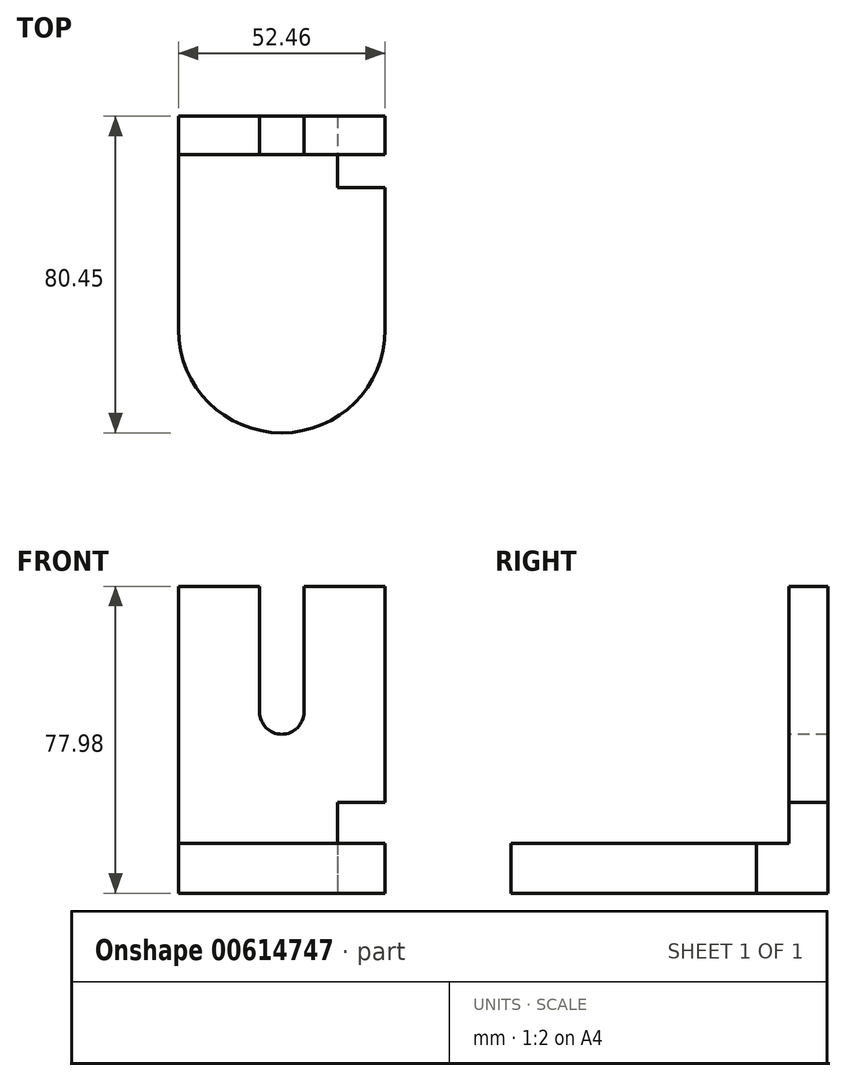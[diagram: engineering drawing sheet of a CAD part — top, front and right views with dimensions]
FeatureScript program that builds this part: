
annotation { "Feature Type Name" : "Feature", "Feature Type Description" : "" }
export const myFeature = defineFeature(function(context is Context, id is Id, definition is map)
    precondition{}
    {
        {
            var Q0;
            Q0=qCreatedBy(makeId("Top.planeOp"),FACE);
            var sketch = newSketch(context, id + "F0", { "sketchPlane" : qUnion([Q0])});
            skLineSegment(sketch, "E0.bottom", {"start": v(26.23, -27.11) * mm, "end": v(-26.23, -27.11) * mm});
            skLineSegment(sketch, "E0.top", {"start": v(26.23, 27.11) * mm, "end": v(-26.23, 27.11) * mm});
            skLineSegment(sketch, "E0.left", {"start": v(26.23, -27.11) * mm, "end": v(26.23, 27.11) * mm});
            skLineSegment(sketch, "E0.right", {"start": v(-26.23, -27.11) * mm, "end": v(-26.23, 27.11) * mm});
            skPoint(sketch, "E0.middle", {"position": v(0, 0) * mm});
            skArc(sketch, "E1", {"start": v(-26.23, -27.11) * mm, "mid": v(0, -53.34) * mm, "end": v(26.23, -27.11) * mm});
            skSolve(sketch);
        }
        {
            var Q0;
            Q0=makeQuery(id+"F0.imprint","IMPRINT",FACE,{"disambiguationData":[TD([[makeQuery(id+"F0.imprint","IMPRINT",EDGE,{"derivedFrom":sQuery(id+"F0.wireOp",EDGE,"E0.bottom")}),-1.0]])]});
            var sketch = newSketch(context, id + "F1", { "sketchPlane" : qUnion([Q0])});
            skSolve(sketch);
        }
        {
            var Q0;
            Q0 = qSketchRegion(id + "F1", true);
            var Q1;
            Q1=makeQuery(id+"F0.imprint","IMPRINT",FACE,{"disambiguationData":[TD([[makeQuery(id+"F0.imprint","IMPRINT",EDGE,{"derivedFrom":sQuery(id+"F0.wireOp",EDGE,"E0.bottom")}),1.0]])]});
            var Q2;
            Q2=makeQuery(id+"F0.imprint","IMPRINT",FACE,{"disambiguationData":[TD([[makeQuery(id+"F0.imprint","IMPRINT",EDGE,{"derivedFrom":sQuery(id+"F0.wireOp",EDGE,"E0.bottom")}),-1.0]])]});
            extrude(context, id + "F2", {"entities" : qUnion([Q0, Q1, Q2]), "depth" : 25.4 * mm, "offsetDistance" : 25.4 * mm});
        }
        {
            var Q0;
            Q0=makeQuery(id+"F2.opExtrude","CAP_FACE",FACE,{"disambiguationData":[OSD([sQuery(id+"F0.wireOp",EDGE,"E0.top"),sQuery(id+"F0.wireOp",EDGE,"E0.left"),sQuery(id+"F0.wireOp",EDGE,"E0.right"),sQuery(id+"F0.wireOp",EDGE,"E1")])],"isStart":false});
            var sketch = newSketch(context, id + "F3", { "sketchPlane" : qUnion([Q0])});
            skLineSegment(sketch, "E2.bottom", {"start": v(26.23, 27.11) * mm, "end": v(-26.23, 27.11) * mm});
            skLineSegment(sketch, "E2.top", {"start": v(26.23, 17.33) * mm, "end": v(-26.23, 17.33) * mm});
            skLineSegment(sketch, "E2.left", {"start": v(26.23, 27.11) * mm, "end": v(26.23, 17.33) * mm});
            skLineSegment(sketch, "E2.right", {"start": v(-26.23, 27.11) * mm, "end": v(-26.23, 17.33) * mm});
            skPoint(sketch, "E2.middle", {"position": v(0, 22.22) * mm});
            skSolve(sketch);
        }
        {
            var Q0;
            Q0=makeQuery(id+"F3.imprint","IMPRINT",FACE,{"disambiguationData":[TD([[makeQuery(id+"F3.imprint","IMPRINT",EDGE,{"derivedFrom":sQuery(id+"F3.wireOp",EDGE,"E2.bottom")}),1.0]])]});
            extrude(context, id + "F4", {"entities" : qUnion([Q0]), "operationType" : NewBodyOperationType.ADD, "depth" : 65.02 * mm, "offsetDistance" : 25.4 * mm});
        }
        {
            var Q0;
            Q0=makeQuery(id+"F1.imprint","IMPRINT",FACE,{"disambiguationData":[TD([[makeQuery(id+"F1.imprint","IMPRINT",EDGE,{"derivedFrom":makeQuery(id+"F0.imprint","IMPRINT",EDGE,{"derivedFrom":sQuery(id+"F0.wireOp",EDGE,"E0.bottom")})}),-1.0]])]});
            var sketch = newSketch(context, id + "F5", { "sketchPlane" : qUnion([Q0])});
            skLineSegment(sketch, "E3.bottom", {"start": v(26.25, 27.14) * mm, "end": v(14.15, 27.14) * mm});
            skLineSegment(sketch, "E3.top", {"start": v(26.25, 8.96) * mm, "end": v(14.15, 8.96) * mm});
            skLineSegment(sketch, "E3.left", {"start": v(26.25, 27.14) * mm, "end": v(26.25, 8.96) * mm});
            skLineSegment(sketch, "E3.right", {"start": v(14.15, 27.14) * mm, "end": v(14.15, 8.96) * mm});
            skSolve(sketch);
        }
        {
            var Q0;
            {var subQ0=sQuery(id+"F5.wireOp",EDGE,"E3.right");var subQ1=sQuery(id+"F5.wireOp",EDGE,"E3.top");var subQ2=makeQuery(id+"F5.imprint","INTERSECT",VERTEX,{"derivedFrom":[subQ1,subQ0]});Q0=makeQuery(id+"F5.imprint","IMPRINT",FACE,{"disambiguationData":[TD([[makeQuery(id+"F5.imprint","IMPRINT",EDGE,{"disambiguationData":[TD([[subQ2,1.0]])],"derivedFrom":subQ1}),-1.0]])]});}
            extrude(context, id + "F6", {"entities" : qUnion([Q0]), "operationType" : NewBodyOperationType.REMOVE, "depth" : 50.8 * mm, "offsetDistance" : 25.4 * mm});
        }
        {
            var Q0;
            Q0=makeQuery(id+"F2.opExtrude","CAP_FACE",FACE,{"disambiguationData":[OSD([sQuery(id+"F0.wireOp",EDGE,"E0.top"),sQuery(id+"F0.wireOp",EDGE,"E0.left"),sQuery(id+"F0.wireOp",EDGE,"E0.right"),sQuery(id+"F0.wireOp",EDGE,"E1")])],"isStart":false});
            extrude(context, id + "F7", {"entities" : qUnion([Q0]), "operationType" : NewBodyOperationType.REMOVE, "oppositeDirection" : true, "depth" : 12.7 * mm, "offsetDistance" : 25.4 * mm});
        }
        {
            var Q0;
            Q0=makeQuery(id+"F4.opExtrude","CAP_FACE",FACE,{"disambiguationData":[OSD([sQuery(id+"F3.wireOp",EDGE,"E2.bottom"),sQuery(id+"F3.wireOp",EDGE,"E2.top"),sQuery(id+"F3.wireOp",EDGE,"E2.left"),sQuery(id+"F3.wireOp",EDGE,"E2.right")])],"isStart":false});
            extrude(context, id + "F8", {"entities" : qUnion([Q0]), "operationType" : NewBodyOperationType.REMOVE, "oppositeDirection" : true, "depth" : 12.45 * mm, "offsetDistance" : 25.4 * mm});
        }
        {
            var Q0;
            Q0=makeQuery(id+"F6.boolean.opBoolean","COPY",FACE,{"derivedFrom":makeQuery(id+"F6.opExtrude","CAP_FACE",FACE,{"disambiguationData":[OSD([sQuery(id+"F0.wireOp",EDGE,"E0.top"),sQuery(id+"F0.wireOp",EDGE,"E0.left"),sQuery(id+"F5.wireOp",EDGE,"E3.top"),sQuery(id+"F5.wireOp",EDGE,"E3.right")])],"isStart":false})});
            extrude(context, id + "F9", {"entities" : qUnion([Q0]), "operationType" : NewBodyOperationType.ADD, "depth" : 27.7 * mm, "offsetDistance" : 25.4 * mm});
        }
        {
            var Q0;
            {var subQ0=sQuery(id+"F3.wireOp",EDGE,"E2.top");Q0=makeQuery(id+"F9.boolean.opBoolean","MERGE",FACE,{"derivedFrom":[makeQuery(id+"F7.boolean.opBoolean","MERGE",FACE,{"derivedFrom":[makeQuery(id+"F4.opExtrude","SWEPT_FACE",FACE,{"disambiguationData":[OSD([subQ0])]}),makeQuery(id+"F7.opExtrude","SWEPT_FACE",FACE,{"disambiguationData":[OSD([subQ0])]})]}),makeQuery(id+"F9.opExtrude","SWEPT_FACE",FACE,{"disambiguationData":[OSD([sQuery(id+"F0.wireOp",EDGE,"E0.top"),sQuery(id+"F0.wireOp",EDGE,"E0.left"),subQ0,sQuery(id+"F5.wireOp",EDGE,"E3.top"),sQuery(id+"F5.wireOp",EDGE,"E3.right")])]})]});}
            var sketch = newSketch(context, id + "F10", { "sketchPlane" : qUnion([Q0])});
            skLineSegment(sketch, "E4.bottom", {"start": v(5.62, 46.04) * mm, "end": v(-5.62, 46.04) * mm});
            skLineSegment(sketch, "E4.top", {"start": v(5.62, 83.12) * mm, "end": v(-5.62, 83.12) * mm});
            skLineSegment(sketch, "E4.left", {"start": v(5.62, 46.04) * mm, "end": v(5.62, 83.12) * mm});
            skLineSegment(sketch, "E4.right", {"start": v(-5.62, 46.04) * mm, "end": v(-5.62, 83.12) * mm});
            skPoint(sketch, "E4.middle", {"position": v(0, 64.58) * mm});
            skArc(sketch, "E5", {"start": v(-5.62, 46.04) * mm, "mid": v(0, 40.42) * mm, "end": v(5.62, 46.04) * mm});
            skSolve(sketch);
        }
        {
            var Q0;
            {var subQ0=sQuery(id+"F10.wireOp",EDGE,"E4.bottom");Q0=makeQuery(id+"F10.imprint","IMPRINT",FACE,{"disambiguationData":[TD([[makeQuery(id+"F10.imprint","IMPRINT",EDGE,{"derivedFrom":subQ0}),-1.0]])]});}
            var Q1;
            Q1=makeQuery(id+"F10.imprint","IMPRINT",FACE,{"disambiguationData":[TD([[makeQuery(id+"F10.imprint","IMPRINT",EDGE,{"derivedFrom":sQuery(id+"F10.wireOp",EDGE,"E4.bottom")}),1.0]])]});
            var Q2;
            {var subQ0=sQuery(id+"F10.wireOp",EDGE,"E4.top");Q2=makeQuery(id+"F10.imprint","IMPRINT",FACE,{"disambiguationData":[TD([[makeQuery(id+"F10.imprint","IMPRINT",EDGE,{"derivedFrom":subQ0}),1.0]])]});}
            extrude(context, id + "F11", {"entities" : qUnion([Q0, Q1, Q2]), "operationType" : NewBodyOperationType.REMOVE, "oppositeDirection" : true, "depth" : 65.28 * mm, "offsetDistance" : 25.4 * mm});
        }
    });
